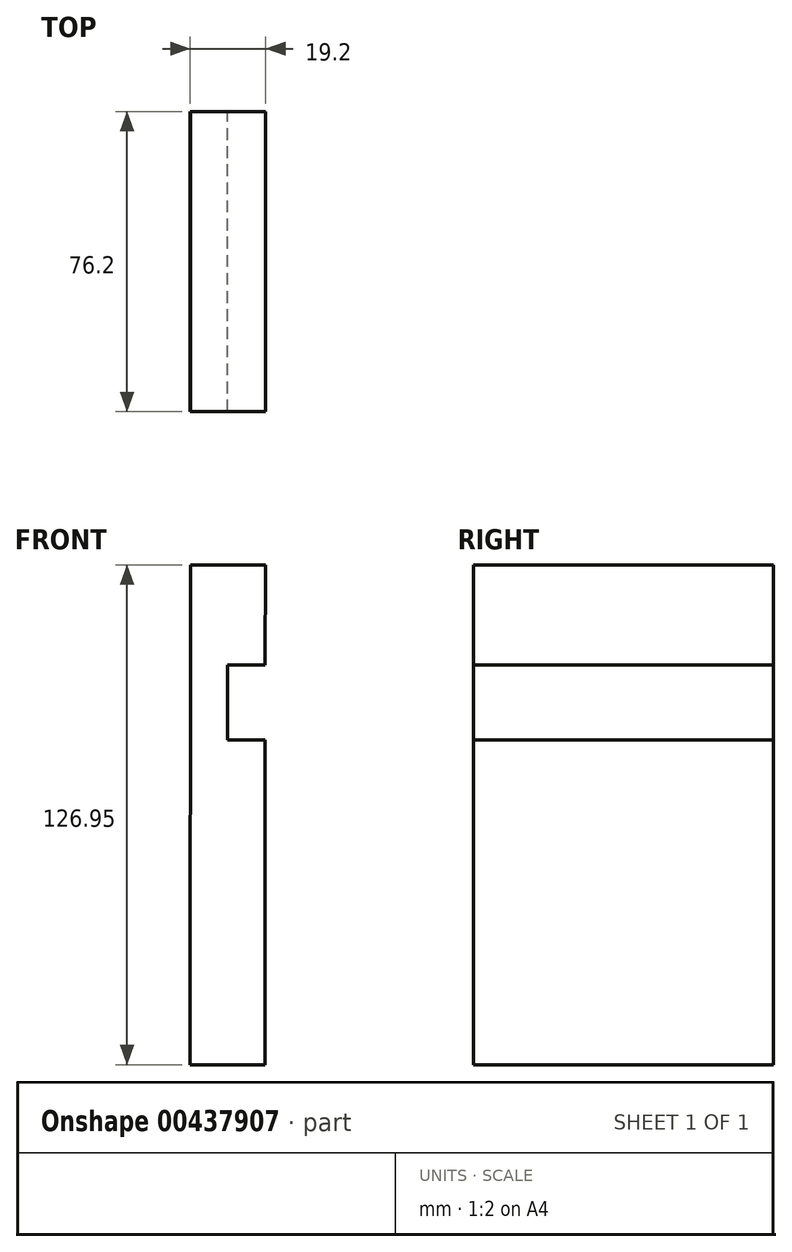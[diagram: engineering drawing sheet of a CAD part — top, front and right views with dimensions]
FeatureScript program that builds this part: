
annotation { "Feature Type Name" : "Feature", "Feature Type Description" : "" }
export const myFeature = defineFeature(function(context is Context, id is Id, definition is map)
    precondition{}
    {
        {
            var Q0;
            Q0=qCreatedBy(makeId("Front.planeOp"),FACE);
            var sketch = newSketch(context, id + "F0", { "sketchPlane" : qUnion([Q0])});
            skLineSegment(sketch, "E0", {"start": v(-18.9, 53.09) * mm, "end": v(0.15, 53.09) * mm});
            skLineSegment(sketch, "E1", {"start": v(0.15, 53.09) * mm, "end": v(0, 27.69) * mm});
            skLineSegment(sketch, "E2", {"start": v(0, 27.69) * mm, "end": v(-9.52, 27.74) * mm});
            skLineSegment(sketch, "E3", {"start": v(-9.52, 27.74) * mm, "end": v(-9.52, 8.7) * mm});
            skLineSegment(sketch, "E4", {"start": v(-9.52, 8.7) * mm, "end": v(0, 8.7) * mm});
            skLineSegment(sketch, "E5", {"start": v(0, 8.7) * mm, "end": v(0, -73.86) * mm});
            skLineSegment(sketch, "E6", {"start": v(0, -73.86) * mm, "end": v(-19.05, -73.86) * mm});
            skLineSegment(sketch, "E7", {"start": v(-19.05, -73.86) * mm, "end": v(-18.9, 53.09) * mm});
            skSolve(sketch);
        }
        {
            var Q0;
            Q0=makeQuery(id+"F0.imprint","IMPRINT",FACE,{"disambiguationData":[TD([[makeQuery(id+"F0.imprint","IMPRINT",EDGE,{"derivedFrom":sQuery(id+"F0.wireOp",EDGE,"E0")}),-1.0]])]});
            extrude(context, id + "F1", {"entities" : qUnion([Q0]), "depth" : 76.2 * mm});
        }
    });
